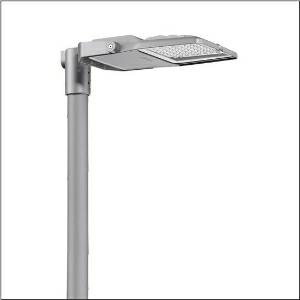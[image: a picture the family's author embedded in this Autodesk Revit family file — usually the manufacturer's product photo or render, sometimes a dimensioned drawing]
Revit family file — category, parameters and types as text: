
# Revit family: floodlight_fl_21_mini___pl52_5xa7776b2d3a_5eef
name_source: partatom
category: Lighting Fixtures
units: mm (PartAtom-declared; Revit-internal decimal feet)

## family parameters
Cut with Voids When Loaded = No
Host = Face
Light Source = No
Part Type = Normal
Room Calculation Point = No
Round Connector Dimension = Use Diameter
Shared = No

## types (1)
- --- (1 x LED, 6230 lm, 45.7 W, 3000K)
    Apparent Load = 46 VA
    CIE Flux Codes = 26 60 98 100 100
    Color Rendering = 70
    Color Temperature = 3000K
    Default Elevation = 1800 mm
    Description = Floodlight FL 21 mini, floodlight, primary light control with lens, of PMMA, primary optical cover: protective disc, of toughened safety glass, transparent, light distribution: PL52, light emission: direct distribution, installation type: surface-mounted, LED, High Power LED, rated luminous flux: 6.230lm, luminous efficacy: 136lm/W, light colour: 730, colour temperature: 3000K, control gear: Smart Interface (Zhaga), control: flexible luminous flux parameterisation, time-dependent luminous flux control, constant luminous flux control, overheat protection, pre-setting: logarithmic dimming characteristic, with terminal, 6-pole, mains connection: 220..240V, AC, 50/60Hz, start of lifetime: 46W, end of service life: 48W, reduction: 22W, luminaire housing, of diecast aluminium, powder-coated, Siteco® metallic grey (DB 702S), corrosivity category C5 mid according to DIN EN ISO 12944, suitable for swimming pools, chlorine-resistant, sealing non-destructively replaceable, please order mast flange separately, mast bracket, of steel, galvanised, powder-coated, Siteco® metallic grey (DB 702S), Smart Interface below and above, protection rating (complete): IP66, insulation class (complete): insulation class II (safety insulation), certification: CE, ENEC, VDE, protection symbol: D, impact resistance: IK08, permissible operating ambient temperature: -40..+40°C, permissible operating ambient temperature for outdoor applications: -40..+50°C, standard: DIN EN 12944, LABS conformity tested according to VDMA 24364:2018-05, packaging unit: 1 piece

Light Distribution: PL52
    Height = 70 mm
    Lamp = 1 x LED
    Lamp Light Flux = 6230 lm
    Lamp Power = 45.7 W
    Lamp count = 1
    Length = 485 mm
    Luminous efficacy = 136 lm/W
    Manufacturer = Siteco
    ModVariant = No
    Model = 5XA7776B2D3A
    Number of Poles = 1
    OnlyDefault = Yes
    Power Factor = 1
    Product Name = Floodlight FL 21 mini | PL52
    Product group = floodlight | pylon annexe
    ProductGroupID = 6200
    Protection Class = Protection class II
    Protection Degree = IP 66
    RLX_Detail_Level = 1
    RLX_Emergency_Light_Flux = 0 lm
    RLX_Emergency_Type = 0
    RLX_Emergency_Type_DB = No
    RlxData = <blob elided: 101253 chars, md5=72208ef3>
    Socket = socket
    Standby Power = 0 W
    System Light Flux = 6230 lm
    System Power = 46 W
    Type Comments = factory setting: luminous flux: 100 % | dim-lin: 254 | 463 mA
    Type Image = l_1007125.jpg
    URL = http://relux.com
    VarID = @adj_163386
    Voltage = 0 V
    Weight = 0.00 kg
    Width = 337 mm

## geometry (parser evidence)
native form markers: Blend x4, Sweep x11
no freeform markers — native parametric forms only
